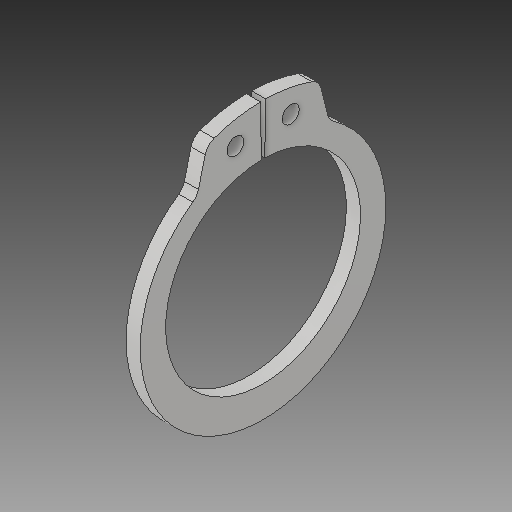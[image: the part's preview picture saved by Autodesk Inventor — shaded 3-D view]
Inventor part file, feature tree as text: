
AUTODESK INVENTOR PART (.ipt)
format: ipt  version: 2017 SP1 (Build 210196100, 196)  size: 110,080 bytes
history: native  units: in
note: dims shown in document units (in); Inventor stores cm internally (conversion verified against a paired STEP export)
features: fillet x1
ambient origin geometry x8: Origin, YZ Plane, XZ Plane, XY Plane, X Axis, Y Axis, Z Axis, Center Point
bodies: Solid1 (feature_tree)
feature tree (1):
  fillet  "Fillet1"  [1 undecoded]
note: 1 required parameter value undecoded (feature->parameter linkage not recoverable at this tier; creation-order binding heuristic only, values carry confidence <= 0.55)
